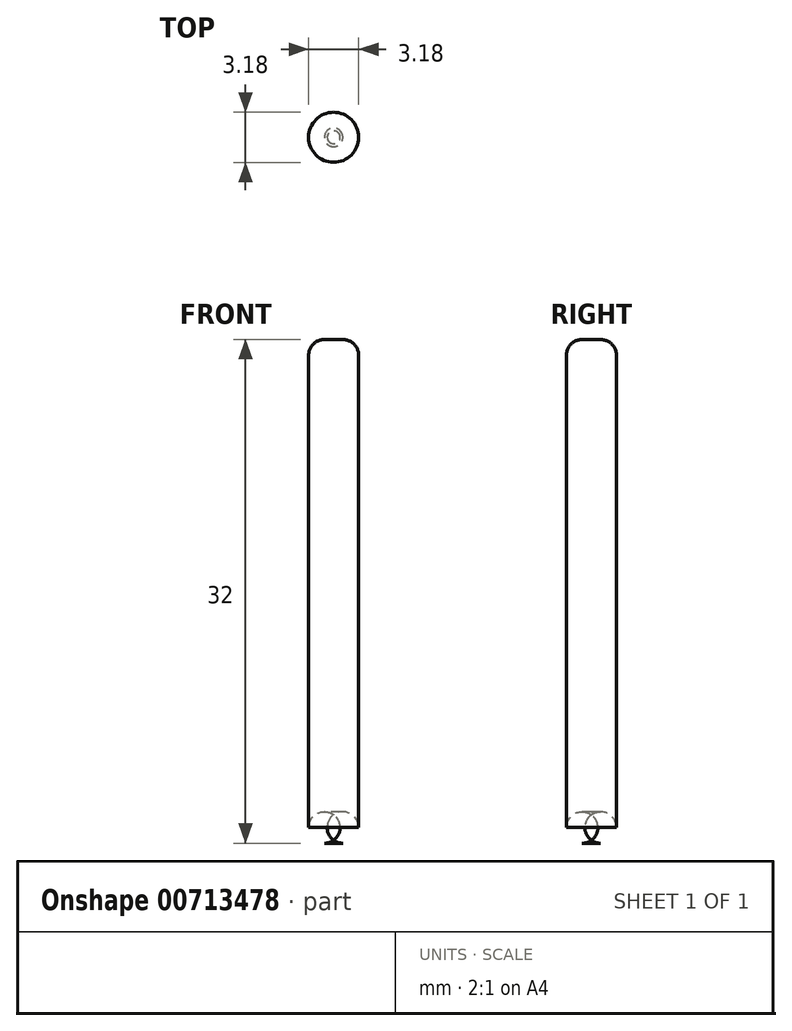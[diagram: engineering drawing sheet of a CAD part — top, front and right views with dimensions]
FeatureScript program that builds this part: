
annotation { "Feature Type Name" : "Feature", "Feature Type Description" : "" }
export const myFeature = defineFeature(function(context is Context, id is Id, definition is map)
    precondition{}
    {
        {
            assignVariable(context, id + "F0", {"name" : "lengthInFrame", "anyValue" : 8 * mm});
        }
        {
            assignVariable(context, id + "F1", {"name" : "lengthPertruding", "anyValue" : 24 * mm});
        }
        {
            assignVariable(context, id + "F2", {"name" : "length", "anyValue" : getVariable(context, 'lengthInFrame') + getVariable(context, 'lengthPertruding')});
        }
        {
            var Q0;
            Q0=qCreatedBy(makeId("Top.planeOp"),FACE);
            var sketch = newSketch(context, id + "F3", { "sketchPlane" : qUnion([Q0])});
            skCircle(sketch, "E0", {"center": v(0, 0) * mm, "radius": 1.59 * mm});
            skSolve(sketch);
        }
        {
            var Q0;
            Q0=qSketchRegion(id+"F3",true);
            extrude(context, id + "F4", {"entities" : qUnion([Q0]), "depth" : getVariable(context, 'length'), "offsetDistance" : 25 * mm});
        }
        {
            var Q0;
            Q0=makeQuery(id+"F4.opExtrude","CAP_EDGE",EDGE,{"disambiguationData":[OSD([sQuery(id+"F3.wireOp",EDGE,"E0")])],"isStart":false});
            var Q1;
            Q1=makeQuery(id+"F4.opExtrude","CAP_EDGE",EDGE,{"disambiguationData":[OSD([sQuery(id+"F3.wireOp",EDGE,"E0")])],"isStart":true});
            fillet(context, id + "F5", {"entities" : qUnion([Q0, Q1]), "radius" : 1 * mm, "tangentPropagation" : true, "allowEdgeOverflow" : false});
        }
    });
